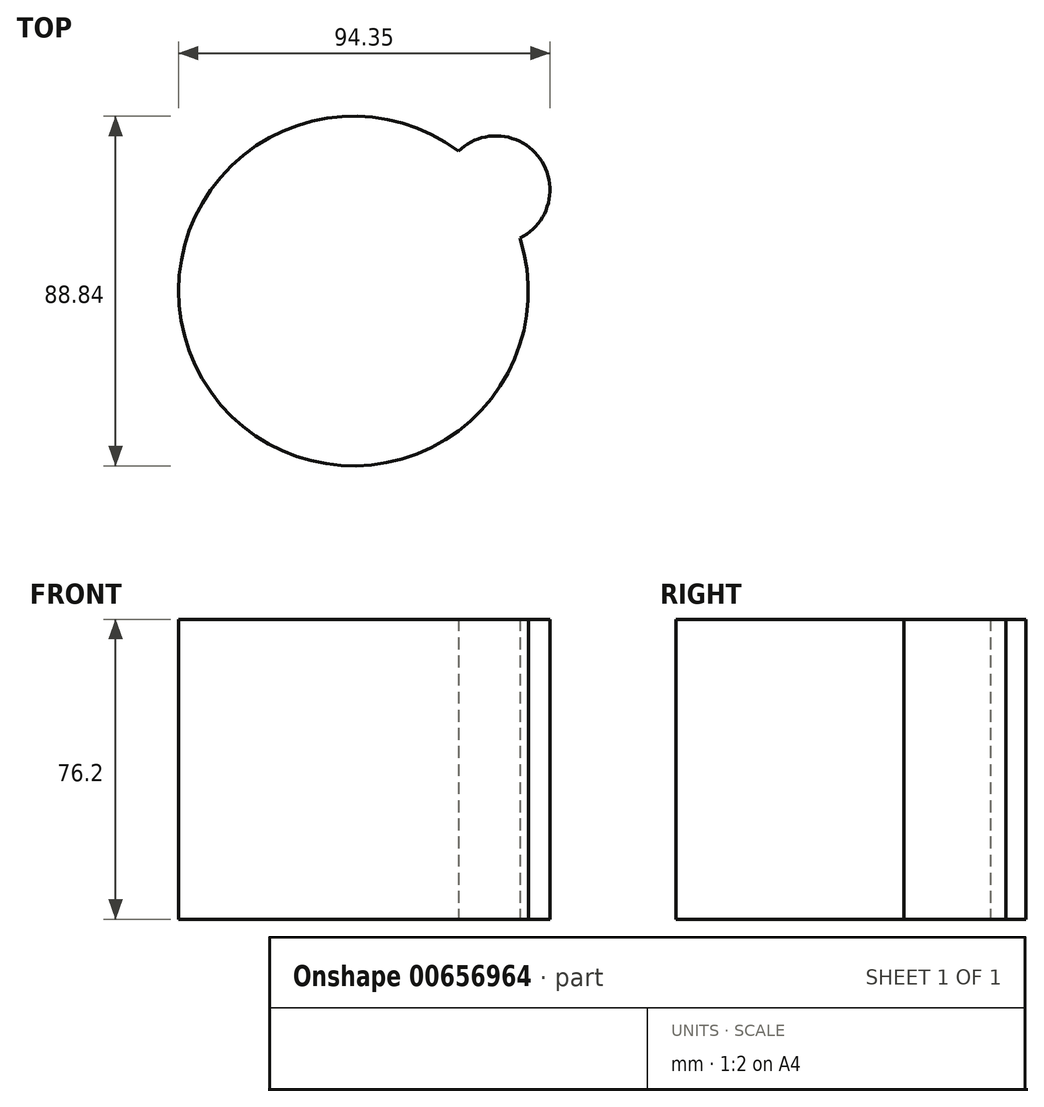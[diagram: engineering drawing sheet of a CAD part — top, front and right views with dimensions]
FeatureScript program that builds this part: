
annotation { "Feature Type Name" : "Feature", "Feature Type Description" : "" }
export const myFeature = defineFeature(function(context is Context, id is Id, definition is map)
    precondition{}
    {
        {
            var Q0;
            Q0=qCreatedBy(makeId("Top.planeOp"),FACE);
            var sketch = newSketch(context, id + "F0", { "sketchPlane" : qUnion([Q0])});
            skCircle(sketch, "E0", {"center": v(-12.26, 5.25) * mm, "radius": 44.42 * mm});
            skCircle(sketch, "E1", {"center": v(23.96, 30.97) * mm, "radius": 13.71 * mm});
            skSolve(sketch);
        }
        {
            var Q0;
            {var subQ0=sQuery(id+"F0.wireOp",EDGE,"E1");var subQ1=sQuery(id+"F0.wireOp",EDGE,"E0");var subQ2=makeQuery(id+"F0.imprint","INTERSECT",VERTEX,{"disambiguationData":[OD(0.0)],"derivedFrom":[subQ1,subQ0]});Q0=makeQuery(id+"F0.imprint","IMPRINT",FACE,{"disambiguationData":[TD([[makeQuery(id+"F0.imprint","IMPRINT",EDGE,{"disambiguationData":[TD([[subQ2,-1.0]])],"derivedFrom":subQ1}),1.0]])]});}
            var Q1;
            {var subQ0=sQuery(id+"F0.wireOp",EDGE,"E1");var subQ1=sQuery(id+"F0.wireOp",EDGE,"E0");var subQ2=makeQuery(id+"F0.imprint","INTERSECT",VERTEX,{"disambiguationData":[OD(0.0)],"derivedFrom":[subQ1,subQ0]});Q1=makeQuery(id+"F0.imprint","IMPRINT",FACE,{"disambiguationData":[TD([[makeQuery(id+"F0.imprint","IMPRINT",EDGE,{"disambiguationData":[TD([[subQ2,1.0]])],"derivedFrom":subQ1}),1.0]])]});}
            var Q2;
            {var subQ0=sQuery(id+"F0.wireOp",EDGE,"E1");var subQ1=sQuery(id+"F0.wireOp",EDGE,"E0");var subQ2=makeQuery(id+"F0.imprint","INTERSECT",VERTEX,{"disambiguationData":[OD(0.0)],"derivedFrom":[subQ1,subQ0]});Q2=makeQuery(id+"F0.imprint","IMPRINT",FACE,{"disambiguationData":[TD([[makeQuery(id+"F0.imprint","IMPRINT",EDGE,{"disambiguationData":[TD([[subQ2,1.0]])],"derivedFrom":subQ1}),-1.0]])]});}
            extrude(context, id + "F1", {"entities" : qUnion([Q0, Q1, Q2]), "depth" : 50.8 * mm, "offsetDistance" : 25.4 * mm});
        }
        {
            var Q0;
            Q0=makeQuery(id+"F1.opExtrude","CAP_FACE",FACE,{"disambiguationData":[OSD([sQuery(id+"F0.wireOp",EDGE,"E0"),sQuery(id+"F0.wireOp",EDGE,"E1")])],"isStart":false});
            var Q1;
            Q1=makeQuery(id+"F1.opExtrude","CAP_FACE",FACE,{"disambiguationData":[OSD([sQuery(id+"F0.wireOp",EDGE,"E0"),sQuery(id+"F0.wireOp",EDGE,"E1")])],"isStart":true});
            extrude(context, id + "F2", {"entities" : qUnion([Q0, Q1]), "operationType" : NewBodyOperationType.ADD, "depth" : 25.4 * mm, "offsetDistance" : 25.4 * mm});
        }
    });
